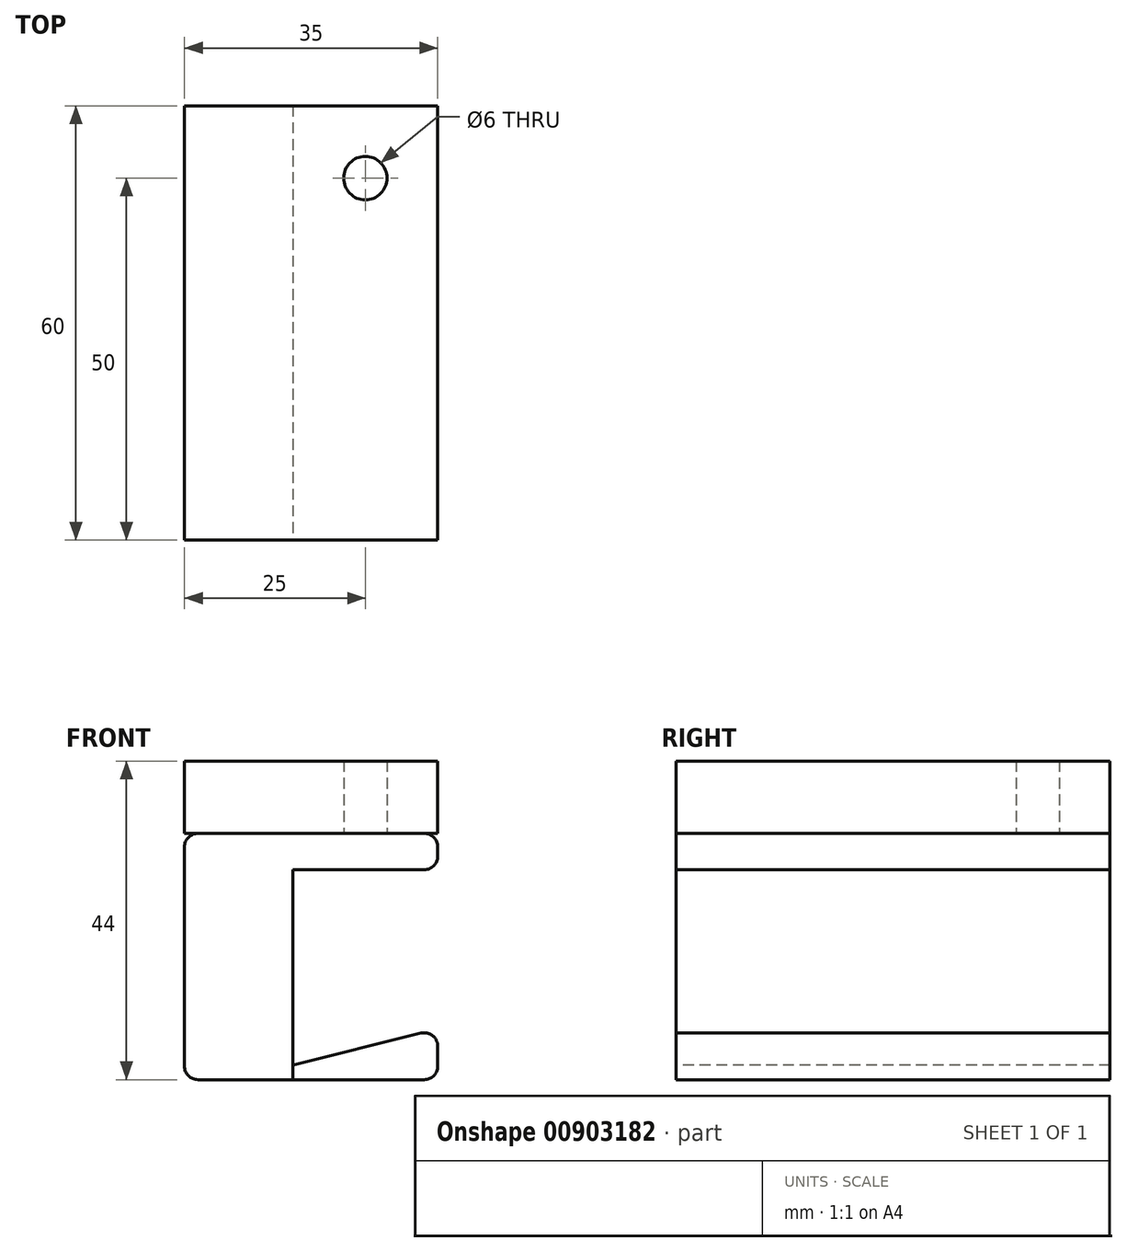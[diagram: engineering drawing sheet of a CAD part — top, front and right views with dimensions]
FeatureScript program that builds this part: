
annotation { "Feature Type Name" : "Feature", "Feature Type Description" : "" }
export const myFeature = defineFeature(function(context is Context, id is Id, definition is map)
    precondition{}
    {
        {
            var Q0;
            Q0=qCreatedBy(makeId("Top.planeOp"),FACE);
            var sketch = newSketch(context, id + "F0", { "sketchPlane" : qUnion([Q0])});
            skLineSegment(sketch, "E0.bottom", {"start": v(-7.5, 30) * mm, "end": v(7.5, 30) * mm});
            skLineSegment(sketch, "E0.top", {"start": v(-7.5, -30) * mm, "end": v(7.5, -30) * mm});
            skLineSegment(sketch, "E0.left", {"start": v(-7.5, 30) * mm, "end": v(-7.5, -30) * mm});
            skLineSegment(sketch, "E0.right", {"start": v(7.5, 30) * mm, "end": v(7.5, -30) * mm});
            skPoint(sketch, "E0.middle", {"position": v(0, 0) * mm});
            skSolve(sketch);
        }
        {
            var Q0;
            Q0=makeQuery(id+"F0.imprint","IMPRINT",FACE,{"disambiguationData":[TD([[makeQuery(id+"F0.imprint","IMPRINT",EDGE,{"derivedFrom":sQuery(id+"F0.wireOp",EDGE,"E0.bottom")}),-1.0]])]});
            extrude(context, id + "F1", {"entities" : qUnion([Q0]), "oppositeDirection" : true, "depth" : 29 * mm, "offsetDistance" : 25 * mm});
        }
        {
            var Q0;
            Q0=makeQuery(id+"F1.opExtrude","CAP_FACE",FACE,{"disambiguationData":[OSD([sQuery(id+"F0.wireOp",EDGE,"E0.bottom"),sQuery(id+"F0.wireOp",EDGE,"E0.top"),sQuery(id+"F0.wireOp",EDGE,"E0.left"),sQuery(id+"F0.wireOp",EDGE,"E0.right")])],"isStart":true});
            var sketch = newSketch(context, id + "F2", { "sketchPlane" : qUnion([Q0])});
            skLineSegment(sketch, "E1", {"start": v(-7.5, 30) * mm, "end": v(-7.5, -30) * mm});
            skLineSegment(sketch, "E2", {"start": v(-7.5, -30) * mm, "end": v(27.5, -30) * mm});
            skLineSegment(sketch, "E3", {"start": v(27.5, -30) * mm, "end": v(27.5, 30) * mm});
            skLineSegment(sketch, "E4", {"start": v(27.5, 30) * mm, "end": v(-7.5, 30) * mm});
            skSolve(sketch);
        }
        {
            var Q0;
            {var subQ0=sQuery(id+"F2.wireOp",EDGE,"E1");Q0=makeQuery(id+"F2.imprint","IMPRINT",FACE,{"disambiguationData":[TD([[makeQuery(id+"F2.imprint","IMPRINT",EDGE,{"derivedFrom":subQ0}),1.0]])]});}
            var Q1;
            {var subQ2=sQuery(id+"F2.wireOp",EDGE,"E3");Q1=makeQuery(id+"F2.imprint","IMPRINT",FACE,{"disambiguationData":[TD([[makeQuery(id+"F2.imprint","IMPRINT",EDGE,{"derivedFrom":subQ2}),1.0]])]});}
            extrude(context, id + "F3", {"entities" : qUnion([Q0, Q1]), "operationType" : NewBodyOperationType.ADD, "depth" : 5 * mm, "offsetDistance" : 25 * mm});
        }
        {
            var Q0;
            Q0=makeQuery(id+"F3.opExtrude","CAP_FACE",FACE,{"disambiguationData":[OSD([sQuery(id+"F2.wireOp",EDGE,"E1"),sQuery(id+"F2.wireOp",EDGE,"E2"),sQuery(id+"F2.wireOp",EDGE,"E3"),sQuery(id+"F2.wireOp",EDGE,"E4")])],"isStart":false});
            var sketch = newSketch(context, id + "F4", { "sketchPlane" : qUnion([Q0])});
            skLineSegment(sketch, "E5", {"start": v(-7.5, 0) * mm, "end": v(27.5, 0) * mm, "construction": true});
            skCircle(sketch, "E6", {"center": v(17.5, -20) * mm, "radius": 3 * mm});
            skLineSegment(sketch, "E7", {"start": v(17.5, -20) * mm, "end": v(17.5, 0) * mm, "construction": true});
            skCircle(sketch, "E8.MirrorC", {"center": v(17.5, 20) * mm, "radius": 3 * mm});
            skSolve(sketch);
        }
        {
            var Q0;
            Q0=makeQuery(id+"F4.imprint","IMPRINT",FACE,{"disambiguationData":[TD([[makeQuery(id+"F4.imprint","IMPRINT",EDGE,{"derivedFrom":sQuery(id+"F4.wireOp",EDGE,"E6")}),1.0]])]});
            var Q1;
            Q1=makeQuery(id+"F4.imprint","IMPRINT",FACE,{"disambiguationData":[TD([[makeQuery(id+"F4.imprint","IMPRINT",EDGE,{"derivedFrom":sQuery(id+"F4.wireOp",EDGE,"E8.MirrorC")}),-1.0]])]});
            extrude(context, id + "F5", {"entities" : qUnion([Q0, Q1]), "depth" : 10 * mm, "offsetDistance" : 25 * mm});
        }
        {
            var Q0;
            Q0=makeQuery(id+"F3.boolean.opBoolean","MERGE",FACE,{"derivedFrom":[makeQuery(id+"F1.opExtrude","SWEPT_FACE",FACE,{"disambiguationData":[OSD([sQuery(id+"F0.wireOp",EDGE,"E0.top")])]}),makeQuery(id+"F3.opExtrude","SWEPT_FACE",FACE,{"disambiguationData":[OSD([sQuery(id+"F2.wireOp",EDGE,"E2")])]})]});
            var sketch = newSketch(context, id + "F6", { "sketchPlane" : qUnion([Q0])});
            skLineSegment(sketch, "E9", {"start": v(7.5, -27) * mm, "end": v(27.5, -22) * mm});
            skLineSegment(sketch, "E10", {"start": v(27.5, -22) * mm, "end": v(27.5, -29) * mm});
            skLineSegment(sketch, "E11", {"start": v(27.5, -29) * mm, "end": v(7.5, -29) * mm});
            skLineSegment(sketch, "E12", {"start": v(7.5, -29) * mm, "end": v(7.5, -27) * mm});
            skPoint(sketch, "E13", {"position": v(27.5, 0) * mm});
            skSolve(sketch);
        }
        {
            var Q0;
            Q0=makeQuery(id+"F6.imprint","IMPRINT",FACE,{"disambiguationData":[TD([[makeQuery(id+"F6.imprint","IMPRINT",EDGE,{"derivedFrom":sQuery(id+"F6.wireOp",EDGE,"E9")}),-1.0]])]});
            var Q1;
            Q1=makeQuery(id+"F3.boolean.opBoolean","MERGE",FACE,{"derivedFrom":[makeQuery(id+"F1.opExtrude","SWEPT_FACE",FACE,{"disambiguationData":[OSD([sQuery(id+"F0.wireOp",EDGE,"E0.bottom")])]}),makeQuery(id+"F3.opExtrude","SWEPT_FACE",FACE,{"disambiguationData":[OSD([sQuery(id+"F2.wireOp",EDGE,"E4")])]})]});
            extrude(context, id + "F7", {"entities" : qUnion([Q0]), "endBound" : BoundingType.UP_TO_SURFACE, "oppositeDirection" : true, "depth" : 25 * mm, "endBoundEntityFace" : qUnion([Q1]), "offsetDistance" : 25 * mm});
        }
        {
            var Q0;
            Q0=makeQuery(id+"F7.opExtrude","SWEPT_EDGE",EDGE,{"disambiguationData":[OSD([sQuery(id+"F6.wireOp",EDGE,"E9"),sQuery(id+"F6.wireOp",EDGE,"E10")])]});
            var Q1;
            Q1=makeQuery(id+"F7.opExtrude","SWEPT_EDGE",EDGE,{"disambiguationData":[OSD([sQuery(id+"F6.wireOp",EDGE,"E10"),sQuery(id+"F6.wireOp",EDGE,"E11")])]});
            var Q2;
            Q2=makeQuery(id+"F3.opExtrude","CAP_EDGE",EDGE,{"disambiguationData":[OSD([sQuery(id+"F2.wireOp",EDGE,"E3")])],"isStart":false});
            var Q3;
            Q3=makeQuery(id+"F3.opExtrude","CAP_EDGE",EDGE,{"disambiguationData":[OSD([sQuery(id+"F2.wireOp",EDGE,"E3")])],"isStart":true});
            var Q4;
            Q4=makeQuery(id+"F3.opExtrude","CAP_EDGE",EDGE,{"disambiguationData":[OSD([sQuery(id+"F2.wireOp",EDGE,"E1")])],"isStart":false});
            var Q5;
            Q5=makeQuery(id+"F1.opExtrude","CAP_EDGE",EDGE,{"disambiguationData":[OSD([sQuery(id+"F0.wireOp",EDGE,"E0.left")])],"isStart":false});
            fillet(context, id + "F8", {"entities" : qUnion([Q0, Q1, Q2, Q3, Q4, Q5]), "radius" : 1.86 * mm, "tangentPropagation" : true, "allowEdgeOverflow" : false});
        }
    });
